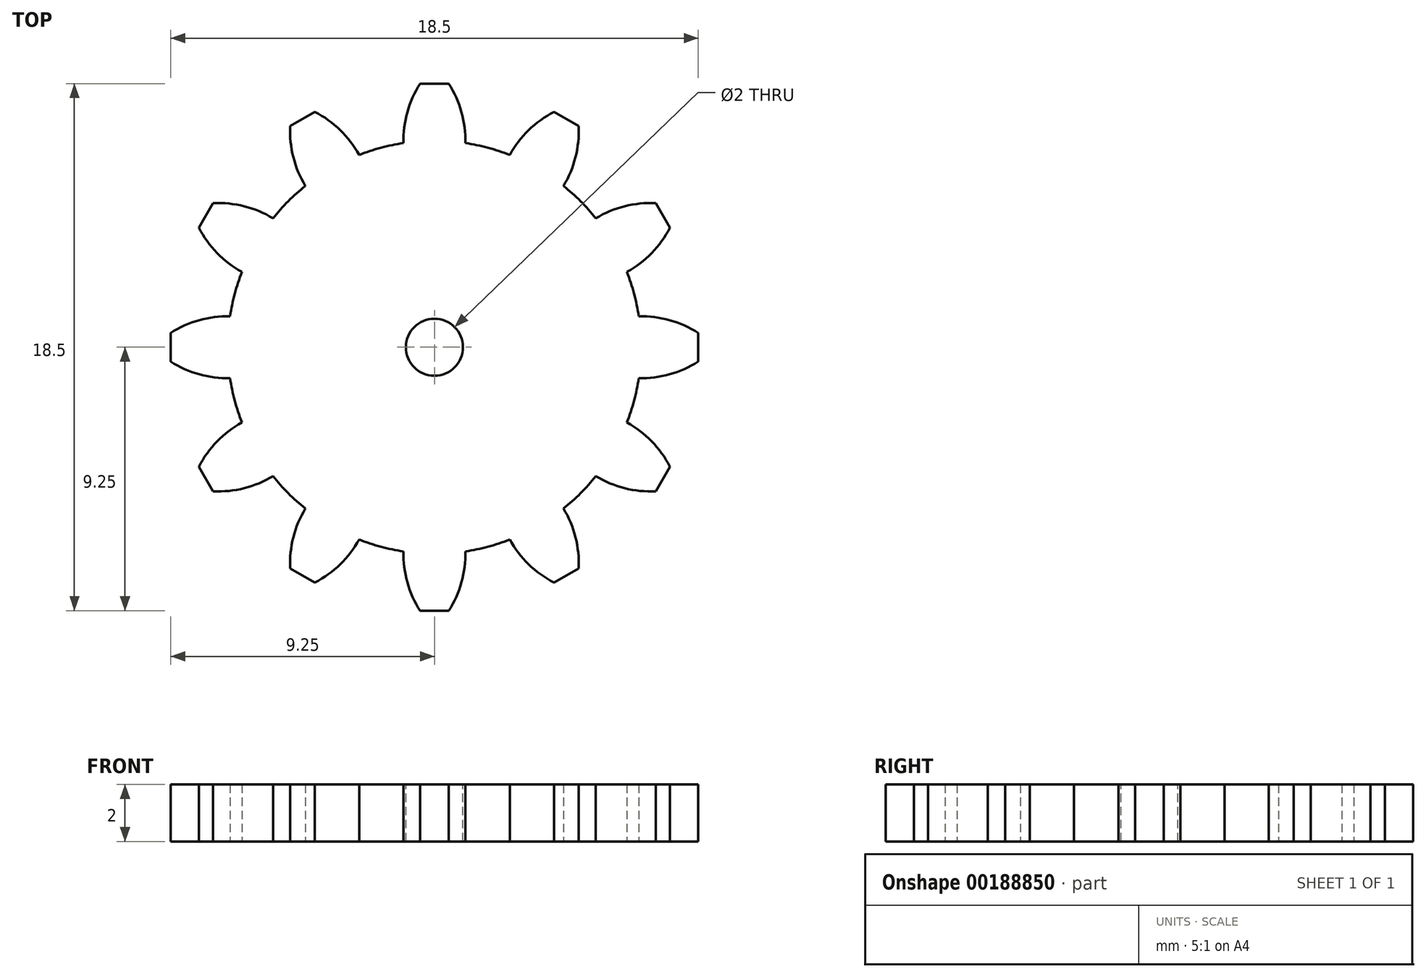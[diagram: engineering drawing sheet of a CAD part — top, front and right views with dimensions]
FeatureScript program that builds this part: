
annotation { "Feature Type Name" : "Feature", "Feature Type Description" : "" }
export const myFeature = defineFeature(function(context is Context, id is Id, definition is map)
    precondition{}
    {
        {
            var Q0;
            Q0=qCreatedBy(makeId("Top.planeOp"),FACE);
            var sketch = newSketch(context, id + "F0", { "sketchPlane" : qUnion([Q0])});
            skCircle(sketch, "E0", {"center": v(0, 0) * mm, "radius": 7.25 * mm});
            skLineSegment(sketch, "E1", {"start": v(0, 0) * mm, "end": v(0, 7.25) * mm, "construction": true});
            skLineSegment(sketch, "E2", {"start": v(0, 9.25) * mm, "end": v(-0.5, 9.25) * mm});
            skArc(sketch, "E3", {"start": v(-0.5, 9.25) * mm, "mid": v(-0.95, 8.25) * mm, "end": v(-1.09, 7.17) * mm});
            skLineSegment(sketch, "E4.MirrorCS", {"start": v(0, 9.25) * mm, "end": v(0.5, 9.25) * mm});
            skArc(sketch, "E5.MirrorCS", {"start": v(0.5, 9.25) * mm, "mid": v(0.95, 8.25) * mm, "end": v(1.09, 7.17) * mm});
            skArc(sketch, "E6.1.0", {"start": v(-5.06, 7.76) * mm, "mid": v(-4.95, 6.67) * mm, "end": v(-4.53, 5.66) * mm});
            skLineSegment(sketch, "E6.1.1", {"start": v(-4.62, 8.01) * mm, "end": v(-5.06, 7.76) * mm});
            skLineSegment(sketch, "E6.1.2", {"start": v(-4.63, 8.01) * mm, "end": v(-4.2, 8.26) * mm});
            skArc(sketch, "E6.1.3", {"start": v(-4.2, 8.26) * mm, "mid": v(-3.3, 7.62) * mm, "end": v(-2.64, 6.75) * mm});
            skArc(sketch, "E6.2.0", {"start": v(-8.26, 4.2) * mm, "mid": v(-7.62, 3.3) * mm, "end": v(-6.75, 2.64) * mm});
            skLineSegment(sketch, "E6.2.1", {"start": v(-8.01, 4.63) * mm, "end": v(-8.26, 4.2) * mm});
            skLineSegment(sketch, "E6.2.2", {"start": v(-8.01, 4.63) * mm, "end": v(-7.76, 5.06) * mm});
            skArc(sketch, "E6.2.3", {"start": v(-7.76, 5.06) * mm, "mid": v(-6.67, 4.95) * mm, "end": v(-5.66, 4.53) * mm});
            skArc(sketch, "E6.3.0", {"start": v(-9.25, -0.5) * mm, "mid": v(-8.25, -0.95) * mm, "end": v(-7.17, -1.09) * mm});
            skLineSegment(sketch, "E6.3.1", {"start": v(-9.25, 0) * mm, "end": v(-9.25, -0.5) * mm});
            skLineSegment(sketch, "E6.3.2", {"start": v(-9.25, 0) * mm, "end": v(-9.25, 0.5) * mm});
            skArc(sketch, "E6.3.3", {"start": v(-9.25, 0.5) * mm, "mid": v(-8.25, 0.95) * mm, "end": v(-7.17, 1.09) * mm});
            skArc(sketch, "E6.4.0", {"start": v(-7.76, -5.06) * mm, "mid": v(-6.67, -4.95) * mm, "end": v(-5.66, -4.53) * mm});
            skLineSegment(sketch, "E6.4.1", {"start": v(-8.01, -4.62) * mm, "end": v(-7.76, -5.06) * mm});
            skLineSegment(sketch, "E6.4.2", {"start": v(-8.01, -4.62) * mm, "end": v(-8.26, -4.2) * mm});
            skArc(sketch, "E6.4.3", {"start": v(-8.26, -4.2) * mm, "mid": v(-7.62, -3.3) * mm, "end": v(-6.75, -2.64) * mm});
            skArc(sketch, "E6.5.0", {"start": v(-4.2, -8.26) * mm, "mid": v(-3.3, -7.62) * mm, "end": v(-2.64, -6.75) * mm});
            skLineSegment(sketch, "E6.5.1", {"start": v(-4.63, -8.01) * mm, "end": v(-4.2, -8.26) * mm});
            skLineSegment(sketch, "E6.5.2", {"start": v(-4.63, -8.01) * mm, "end": v(-5.06, -7.76) * mm});
            skArc(sketch, "E6.5.3", {"start": v(-5.06, -7.76) * mm, "mid": v(-4.95, -6.67) * mm, "end": v(-4.53, -5.66) * mm});
            skArc(sketch, "E6.6.0", {"start": v(0.5, -9.25) * mm, "mid": v(0.95, -8.25) * mm, "end": v(1.09, -7.17) * mm});
            skLineSegment(sketch, "E6.6.1", {"start": v(0, -9.25) * mm, "end": v(0.5, -9.25) * mm});
            skLineSegment(sketch, "E6.6.2", {"start": v(0, -9.25) * mm, "end": v(-0.5, -9.25) * mm});
            skArc(sketch, "E6.6.3", {"start": v(-0.5, -9.25) * mm, "mid": v(-0.95, -8.25) * mm, "end": v(-1.09, -7.17) * mm});
            skArc(sketch, "E6.7.0", {"start": v(5.06, -7.76) * mm, "mid": v(4.95, -6.67) * mm, "end": v(4.53, -5.66) * mm});
            skLineSegment(sketch, "E6.7.1", {"start": v(4.62, -8.01) * mm, "end": v(5.06, -7.76) * mm});
            skLineSegment(sketch, "E6.7.2", {"start": v(4.62, -8.01) * mm, "end": v(4.2, -8.26) * mm});
            skArc(sketch, "E6.7.3", {"start": v(4.2, -8.26) * mm, "mid": v(3.3, -7.62) * mm, "end": v(2.64, -6.75) * mm});
            skArc(sketch, "E6.8.0", {"start": v(8.26, -4.2) * mm, "mid": v(7.62, -3.3) * mm, "end": v(6.75, -2.64) * mm});
            skLineSegment(sketch, "E6.8.1", {"start": v(8.01, -4.63) * mm, "end": v(8.26, -4.2) * mm});
            skLineSegment(sketch, "E6.8.2", {"start": v(8.01, -4.63) * mm, "end": v(7.76, -5.06) * mm});
            skArc(sketch, "E6.8.3", {"start": v(7.76, -5.06) * mm, "mid": v(6.67, -4.95) * mm, "end": v(5.66, -4.53) * mm});
            skArc(sketch, "E6.9.0", {"start": v(9.25, 0.5) * mm, "mid": v(8.25, 0.95) * mm, "end": v(7.17, 1.09) * mm});
            skLineSegment(sketch, "E6.9.1", {"start": v(9.25, 0) * mm, "end": v(9.25, 0.5) * mm});
            skLineSegment(sketch, "E6.9.2", {"start": v(9.25, 0) * mm, "end": v(9.25, -0.5) * mm});
            skArc(sketch, "E6.9.3", {"start": v(9.25, -0.5) * mm, "mid": v(8.25, -0.95) * mm, "end": v(7.17, -1.09) * mm});
            skArc(sketch, "E6.10.0", {"start": v(7.76, 5.06) * mm, "mid": v(6.67, 4.95) * mm, "end": v(5.66, 4.53) * mm});
            skLineSegment(sketch, "E6.10.1", {"start": v(8.01, 4.62) * mm, "end": v(7.76, 5.06) * mm});
            skLineSegment(sketch, "E6.10.2", {"start": v(8.01, 4.62) * mm, "end": v(8.26, 4.2) * mm});
            skArc(sketch, "E6.10.3", {"start": v(8.26, 4.2) * mm, "mid": v(7.62, 3.3) * mm, "end": v(6.75, 2.64) * mm});
            skArc(sketch, "E6.11.0", {"start": v(4.2, 8.26) * mm, "mid": v(3.3, 7.62) * mm, "end": v(2.64, 6.75) * mm});
            skLineSegment(sketch, "E6.11.1", {"start": v(4.63, 8.01) * mm, "end": v(4.2, 8.26) * mm});
            skLineSegment(sketch, "E6.11.2", {"start": v(4.62, 8.01) * mm, "end": v(5.06, 7.76) * mm});
            skArc(sketch, "E6.11.3", {"start": v(5.06, 7.76) * mm, "mid": v(4.95, 6.67) * mm, "end": v(4.53, 5.66) * mm});
            skSolve(sketch);
        }
        {
            var Q0;
            Q0=qSketchRegion(id+"F0",true);
            extrude(context, id + "F1", {"entities" : qUnion([Q0]), "depth" : 2 * mm});
        }
        {
            var Q0;
            Q0=makeQuery(id+"F1.opExtrude","CAP_FACE",FACE,{"disambiguationData":[OSD([sQuery(id+"F0.wireOp",EDGE,"E0"),sQuery(id+"F0.wireOp",EDGE,"E2"),sQuery(id+"F0.wireOp",EDGE,"E3"),sQuery(id+"F0.wireOp",EDGE,"E4.MirrorCS"),sQuery(id+"F0.wireOp",EDGE,"E5.MirrorCS"),sQuery(id+"F0.wireOp",EDGE,"E6.1.0"),sQuery(id+"F0.wireOp",EDGE,"E6.1.1"),sQuery(id+"F0.wireOp",EDGE,"E6.1.2"),sQuery(id+"F0.wireOp",EDGE,"E6.1.3"),sQuery(id+"F0.wireOp",EDGE,"E6.2.0"),sQuery(id+"F0.wireOp",EDGE,"E6.2.1"),sQuery(id+"F0.wireOp",EDGE,"E6.2.2"),sQuery(id+"F0.wireOp",EDGE,"E6.2.3"),sQuery(id+"F0.wireOp",EDGE,"E6.3.0"),sQuery(id+"F0.wireOp",EDGE,"E6.3.1"),sQuery(id+"F0.wireOp",EDGE,"E6.3.2"),sQuery(id+"F0.wireOp",EDGE,"E6.3.3"),sQuery(id+"F0.wireOp",EDGE,"E6.4.0"),sQuery(id+"F0.wireOp",EDGE,"E6.4.1"),sQuery(id+"F0.wireOp",EDGE,"E6.4.2"),sQuery(id+"F0.wireOp",EDGE,"E6.4.3"),sQuery(id+"F0.wireOp",EDGE,"E6.5.0"),sQuery(id+"F0.wireOp",EDGE,"E6.5.1"),sQuery(id+"F0.wireOp",EDGE,"E6.5.2"),sQuery(id+"F0.wireOp",EDGE,"E6.5.3"),sQuery(id+"F0.wireOp",EDGE,"E6.6.0"),sQuery(id+"F0.wireOp",EDGE,"E6.6.1"),sQuery(id+"F0.wireOp",EDGE,"E6.6.2"),sQuery(id+"F0.wireOp",EDGE,"E6.6.3"),sQuery(id+"F0.wireOp",EDGE,"E6.7.0"),sQuery(id+"F0.wireOp",EDGE,"E6.7.1"),sQuery(id+"F0.wireOp",EDGE,"E6.7.2"),sQuery(id+"F0.wireOp",EDGE,"E6.7.3"),sQuery(id+"F0.wireOp",EDGE,"E6.8.0"),sQuery(id+"F0.wireOp",EDGE,"E6.8.1"),sQuery(id+"F0.wireOp",EDGE,"E6.8.2"),sQuery(id+"F0.wireOp",EDGE,"E6.8.3"),sQuery(id+"F0.wireOp",EDGE,"E6.9.0"),sQuery(id+"F0.wireOp",EDGE,"E6.9.1"),sQuery(id+"F0.wireOp",EDGE,"E6.9.2"),sQuery(id+"F0.wireOp",EDGE,"E6.9.3"),sQuery(id+"F0.wireOp",EDGE,"E6.10.0"),sQuery(id+"F0.wireOp",EDGE,"E6.10.1"),sQuery(id+"F0.wireOp",EDGE,"E6.10.2"),sQuery(id+"F0.wireOp",EDGE,"E6.10.3"),sQuery(id+"F0.wireOp",EDGE,"E6.11.0"),sQuery(id+"F0.wireOp",EDGE,"E6.11.1"),sQuery(id+"F0.wireOp",EDGE,"E6.11.2"),sQuery(id+"F0.wireOp",EDGE,"E6.11.3"),sQuery(id+"F0.wireOp",EDGE,"E6.12.0"),sQuery(id+"F0.wireOp",EDGE,"E6.12.1"),sQuery(id+"F0.wireOp",EDGE,"E6.12.2"),sQuery(id+"F0.wireOp",EDGE,"E6.12.3"),sQuery(id+"F0.wireOp",EDGE,"E6.13.0"),sQuery(id+"F0.wireOp",EDGE,"E6.13.1"),sQuery(id+"F0.wireOp",EDGE,"E6.13.2"),sQuery(id+"F0.wireOp",EDGE,"E6.13.3"),sQuery(id+"F0.wireOp",EDGE,"E6.14.0"),sQuery(id+"F0.wireOp",EDGE,"E6.14.1"),sQuery(id+"F0.wireOp",EDGE,"E6.14.2"),sQuery(id+"F0.wireOp",EDGE,"E6.14.3"),sQuery(id+"F0.wireOp",EDGE,"E6.15.0"),sQuery(id+"F0.wireOp",EDGE,"E6.15.1"),sQuery(id+"F0.wireOp",EDGE,"E6.15.2"),sQuery(id+"F0.wireOp",EDGE,"E6.15.3")])],"isStart":false});
            var sketch = newSketch(context, id + "F2", { "sketchPlane" : qUnion([Q0])});
            skCircle(sketch, "E7", {"center": v(0, 0) * mm, "radius": 1 * mm});
            skSolve(sketch);
        }
        {
            var Q0;
            Q0=qSketchRegion(id+"F2",true);
            extrude(context, id + "F3", {"entities" : qUnion([Q0]), "operationType" : NewBodyOperationType.REMOVE, "endBound" : BoundingType.THROUGH_ALL, "oppositeDirection" : true, "depth" : 25 * mm});
        }
    });
